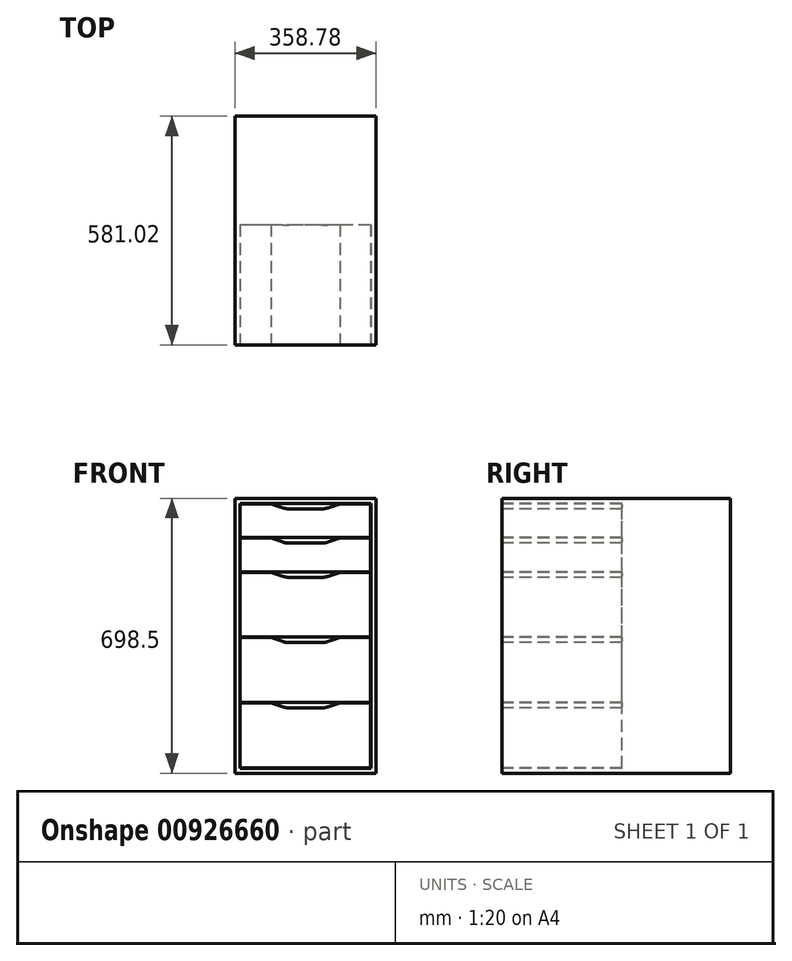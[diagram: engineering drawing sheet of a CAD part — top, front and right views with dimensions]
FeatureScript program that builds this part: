
annotation { "Feature Type Name" : "Feature", "Feature Type Description" : "" }
export const myFeature = defineFeature(function(context is Context, id is Id, definition is map)
    precondition{}
    {
        {
            var Q0;
            Q0=qCreatedBy(makeId("Front.planeOp"),FACE);
            var sketch = newSketch(context, id + "F0", { "sketchPlane" : qUnion([Q0])});
            skLineSegment(sketch, "E0.bottom", {"start": v(-48.77, 656.75) * mm, "end": v(310, 656.75) * mm});
            skLineSegment(sketch, "E0.top", {"start": v(-48.77, -41.75) * mm, "end": v(310, -41.75) * mm});
            skLineSegment(sketch, "E0.left", {"start": v(-48.77, 656.75) * mm, "end": v(-48.77, -41.75) * mm});
            skLineSegment(sketch, "E0.right", {"start": v(310, 656.75) * mm, "end": v(310, -41.75) * mm});
            skSolve(sketch);
        }
        {
            var Q0;
            Q0=makeQuery(id+"F0.imprint","IMPRINT",FACE,{"disambiguationData":[TD([[makeQuery(id+"F0.imprint","IMPRINT",EDGE,{"derivedFrom":sQuery(id+"F0.wireOp",EDGE,"E0.bottom")}),-1.0]])]});
            extrude(context, id + "F1", {"entities" : qUnion([Q0]), "depth" : 581.02 * mm, "offsetDistance" : 25.4 * mm});
        }
        {
            var Q0;
            Q0=makeQuery(id+"F1.opExtrude","CAP_FACE",FACE,{"disambiguationData":[OSD([sQuery(id+"F0.wireOp",EDGE,"E0.bottom"),sQuery(id+"F0.wireOp",EDGE,"E0.top"),sQuery(id+"F0.wireOp",EDGE,"E0.left"),sQuery(id+"F0.wireOp",EDGE,"E0.right")])],"isStart":false});
            var sketch = newSketch(context, id + "F2", { "sketchPlane" : qUnion([Q0])});
            skLineSegment(sketch, "E1.bottom", {"start": v(297.3, -29.05) * mm, "end": v(-36.07, -29.05) * mm});
            skLineSegment(sketch, "E1.top", {"start": v(297.3, 644.05) * mm, "end": v(-36.07, 644.05) * mm});
            skLineSegment(sketch, "E1.left", {"start": v(297.3, -29.05) * mm, "end": v(297.3, 644.05) * mm});
            skLineSegment(sketch, "E1.right", {"start": v(-36.07, -29.05) * mm, "end": v(-36.07, 644.05) * mm});
            skPoint(sketch, "E1.middle", {"position": v(130.62, 307.5) * mm});
            skLineSegment(sketch, "E2.bottom", {"start": v(296.04, -27.78) * mm, "end": v(-34.8, -27.78) * mm});
            skLineSegment(sketch, "E2.top", {"start": v(296.04, 642.78) * mm, "end": v(-34.8, 642.78) * mm});
            skLineSegment(sketch, "E2.left", {"start": v(296.04, -27.78) * mm, "end": v(296.04, 642.78) * mm});
            skLineSegment(sketch, "E2.right", {"start": v(-34.8, -27.78) * mm, "end": v(-34.8, 642.78) * mm});
            skSolve(sketch);
        }
        {
            var Q0;
            Q0 = qSketchRegion(id + "F2", true);
            extrude(context, id + "F3", {"entities" : qUnion([Q0]), "operationType" : NewBodyOperationType.REMOVE, "oppositeDirection" : true, "depth" : 304.8 * mm, "offsetDistance" : 25.4 * mm});
        }
        {
            var Q0;
            Q0=makeQuery(id+"F3.boolean.opBoolean","SPLIT",FACE,{"disambiguationData":[TD([makeQuery(id+"F3.opExtrude","SWEPT_FACE",FACE,{"disambiguationData":[OSD([sQuery(id+"F2.wireOp",EDGE,"E2.bottom")])]})])],"derivedFrom":makeQuery(id+"F1.opExtrude","CAP_FACE",FACE,{"disambiguationData":[OSD([sQuery(id+"F0.wireOp",EDGE,"E0.bottom"),sQuery(id+"F0.wireOp",EDGE,"E0.top"),sQuery(id+"F0.wireOp",EDGE,"E0.left"),sQuery(id+"F0.wireOp",EDGE,"E0.right")])],"isStart":false})});
            var sketch = newSketch(context, id + "F4", { "sketchPlane" : qUnion([Q0])});
            skLineSegment(sketch, "E3.bottom", {"start": v(296.04, 555.79) * mm, "end": v(-34.8, 555.79) * mm});
            skLineSegment(sketch, "E3.top", {"start": v(296.04, 557.06) * mm, "end": v(-34.8, 557.06) * mm});
            skLineSegment(sketch, "E3.left", {"start": v(296.04, 555.79) * mm, "end": v(296.04, 557.06) * mm});
            skLineSegment(sketch, "E3.right", {"start": v(-34.8, 555.79) * mm, "end": v(-34.8, 557.06) * mm});
            skPoint(sketch, "E3.middle", {"position": v(130.62, 556.42) * mm});
            skLineSegment(sketch, "E4.bottom", {"start": v(297.3, 468.8) * mm, "end": v(-36.07, 468.8) * mm});
            skLineSegment(sketch, "E4.top", {"start": v(297.3, 470.06) * mm, "end": v(-36.07, 470.06) * mm});
            skLineSegment(sketch, "E4.left", {"start": v(297.3, 468.8) * mm, "end": v(297.3, 470.06) * mm});
            skLineSegment(sketch, "E4.right", {"start": v(-36.07, 468.8) * mm, "end": v(-36.07, 470.06) * mm});
            skPoint(sketch, "E4.middle", {"position": v(130.62, 469.43) * mm});
            skLineSegment(sketch, "E5.bottom", {"start": v(296.04, 302.93) * mm, "end": v(-36.07, 302.93) * mm});
            skLineSegment(sketch, "E5.top", {"start": v(296.04, 304.2) * mm, "end": v(-36.07, 304.2) * mm});
            skLineSegment(sketch, "E5.left", {"start": v(296.04, 302.93) * mm, "end": v(296.04, 304.2) * mm});
            skLineSegment(sketch, "E5.right", {"start": v(-36.07, 302.93) * mm, "end": v(-36.07, 304.2) * mm});
            skPoint(sketch, "E5.middle", {"position": v(129.98, 303.56) * mm});
            skLineSegment(sketch, "E6.bottom", {"start": v(297.3, 137.07) * mm, "end": v(-34.8, 137.07) * mm});
            skLineSegment(sketch, "E6.top", {"start": v(297.3, 138.34) * mm, "end": v(-34.8, 138.34) * mm});
            skLineSegment(sketch, "E6.left", {"start": v(297.3, 137.07) * mm, "end": v(297.3, 138.34) * mm});
            skLineSegment(sketch, "E6.right", {"start": v(-34.8, 137.07) * mm, "end": v(-34.8, 138.34) * mm});
            skPoint(sketch, "E6.middle", {"position": v(131.25, 137.7) * mm});
            skSolve(sketch);
        }
        {
            var Q0;
            Q0 = qSketchRegion(id + "F4", true);
            extrude(context, id + "F5", {"entities" : qUnion([Q0]), "operationType" : NewBodyOperationType.REMOVE, "oppositeDirection" : true, "depth" : 304.8 * mm, "offsetDistance" : 25.4 * mm});
        }
        {
            var Q0;
            {var subQ0=makeQuery(id+"F3.opExtrude","SWEPT_FACE",FACE,{"disambiguationData":[OSD([sQuery(id+"F2.wireOp",EDGE,"E2.top")])]});Q0=makeQuery(id+"F5.boolean.opBoolean","SPLIT",FACE,{"disambiguationData":[TD([makeQuery(id+"F3.boolean.opBoolean","COPY",FACE,{"derivedFrom":subQ0})])],"derivedFrom":makeQuery(id+"F3.boolean.opBoolean","SPLIT",FACE,{"disambiguationData":[TD([makeQuery(id+"F3.opExtrude","SWEPT_FACE",FACE,{"disambiguationData":[OSD([sQuery(id+"F2.wireOp",EDGE,"E2.bottom")])]})])],"derivedFrom":makeQuery(id+"F1.opExtrude","CAP_FACE",FACE,{"disambiguationData":[OSD([sQuery(id+"F0.wireOp",EDGE,"E0.bottom"),sQuery(id+"F0.wireOp",EDGE,"E0.top"),sQuery(id+"F0.wireOp",EDGE,"E0.left"),sQuery(id+"F0.wireOp",EDGE,"E0.right")])],"isStart":false})})});}
            var sketch = newSketch(context, id + "F6", { "sketchPlane" : qUnion([Q0])});
            skLineSegment(sketch, "E7", {"start": v(43.15, 642.78) * mm, "end": v(218.09, 642.78) * mm});
            skLineSegment(sketch, "E8", {"start": v(218.09, 642.78) * mm, "end": v(179.99, 630.08) * mm});
            skLineSegment(sketch, "E9", {"start": v(179.99, 630.08) * mm, "end": v(81.25, 630.08) * mm});
            skLineSegment(sketch, "E10", {"start": v(81.25, 630.08) * mm, "end": v(43.15, 642.78) * mm});
            skSolve(sketch);
        }
        {
            var Q0;
            Q0 = qSketchRegion(id + "F6", true);
            extrude(context, id + "F7", {"entities" : qUnion([Q0]), "operationType" : NewBodyOperationType.REMOVE, "oppositeDirection" : true, "depth" : 304.8 * mm, "offsetDistance" : 25.4 * mm});
        }
        {
            var Q0;
            Q0=makeQuery(id+"F7.boolean.opBoolean","COPY",EDGE,{"derivedFrom":makeQuery(id+"F7.opExtrude","SWEPT_EDGE",EDGE,{"disambiguationData":[OSD([sQuery(id+"F2.wireOp",EDGE,"E2.top"),sQuery(id+"F6.wireOp",EDGE,"E7"),sQuery(id+"F6.wireOp",EDGE,"E10")])]})});
            var Q1;
            Q1=makeQuery(id+"F7.boolean.opBoolean","COPY",EDGE,{"derivedFrom":makeQuery(id+"F7.opExtrude","SWEPT_EDGE",EDGE,{"disambiguationData":[OSD([sQuery(id+"F6.wireOp",EDGE,"E9"),sQuery(id+"F6.wireOp",EDGE,"E10")])]})});
            var Q2;
            Q2=makeQuery(id+"F7.boolean.opBoolean","COPY",EDGE,{"derivedFrom":makeQuery(id+"F7.opExtrude","SWEPT_EDGE",EDGE,{"disambiguationData":[OSD([sQuery(id+"F6.wireOp",EDGE,"E8"),sQuery(id+"F6.wireOp",EDGE,"E9")])]})});
            var Q3;
            Q3=makeQuery(id+"F7.boolean.opBoolean","COPY",EDGE,{"derivedFrom":makeQuery(id+"F7.opExtrude","SWEPT_EDGE",EDGE,{"disambiguationData":[OSD([sQuery(id+"F2.wireOp",EDGE,"E2.top"),sQuery(id+"F6.wireOp",EDGE,"E7"),sQuery(id+"F6.wireOp",EDGE,"E8")])]})});
            fillet(context, id + "F8", {"entities" : qUnion([Q0, Q1, Q2, Q3]), "radius" : 50.8 * mm, "tangentPropagation" : true, "allowEdgeOverflow" : false});
        }
        {
            var Q0;
            Q0=makeQuery(id+"F5.boolean.opBoolean","SPLIT",FACE,{"disambiguationData":[TD([makeQuery(id+"F5.opExtrude","SWEPT_FACE",FACE,{"disambiguationData":[OSD([sQuery(id+"F4.wireOp",EDGE,"E3.bottom")])]})])],"derivedFrom":makeQuery(id+"F3.boolean.opBoolean","SPLIT",FACE,{"disambiguationData":[TD([makeQuery(id+"F3.opExtrude","SWEPT_FACE",FACE,{"disambiguationData":[OSD([sQuery(id+"F2.wireOp",EDGE,"E2.bottom")])]})])],"derivedFrom":makeQuery(id+"F1.opExtrude","CAP_FACE",FACE,{"disambiguationData":[OSD([sQuery(id+"F0.wireOp",EDGE,"E0.bottom"),sQuery(id+"F0.wireOp",EDGE,"E0.top"),sQuery(id+"F0.wireOp",EDGE,"E0.left"),sQuery(id+"F0.wireOp",EDGE,"E0.right")])],"isStart":false})})});
            var sketch = newSketch(context, id + "F9", { "sketchPlane" : qUnion([Q0])});
            skLineSegment(sketch, "E11", {"start": v(43.15, 555.79) * mm, "end": v(218.09, 555.79) * mm});
            skLineSegment(sketch, "E12", {"start": v(218.09, 555.79) * mm, "end": v(179.99, 543.09) * mm});
            skLineSegment(sketch, "E13", {"start": v(179.99, 543.09) * mm, "end": v(81.25, 543.09) * mm});
            skLineSegment(sketch, "E14", {"start": v(81.25, 543.09) * mm, "end": v(43.15, 555.79) * mm});
            skSolve(sketch);
        }
        {
            var Q0;
            Q0 = qSketchRegion(id + "F9", true);
            extrude(context, id + "F10", {"entities" : qUnion([Q0]), "operationType" : NewBodyOperationType.REMOVE, "oppositeDirection" : true, "depth" : 304.8 * mm, "offsetDistance" : 25.4 * mm});
        }
        {
            var Q0;
            Q0=makeQuery(id+"F10.boolean.opBoolean","COPY",EDGE,{"derivedFrom":makeQuery(id+"F10.opExtrude","SWEPT_EDGE",EDGE,{"disambiguationData":[OSD([sQuery(id+"F4.wireOp",EDGE,"E3.bottom"),sQuery(id+"F9.wireOp",EDGE,"E11"),sQuery(id+"F9.wireOp",EDGE,"E14")])]})});
            var Q1;
            Q1=makeQuery(id+"F10.boolean.opBoolean","COPY",EDGE,{"derivedFrom":makeQuery(id+"F10.opExtrude","SWEPT_EDGE",EDGE,{"disambiguationData":[OSD([sQuery(id+"F9.wireOp",EDGE,"E13"),sQuery(id+"F9.wireOp",EDGE,"E14")])]})});
            var Q2;
            Q2=makeQuery(id+"F10.boolean.opBoolean","COPY",EDGE,{"derivedFrom":makeQuery(id+"F10.opExtrude","SWEPT_EDGE",EDGE,{"disambiguationData":[OSD([sQuery(id+"F4.wireOp",EDGE,"E3.bottom"),sQuery(id+"F9.wireOp",EDGE,"E11"),sQuery(id+"F9.wireOp",EDGE,"E12")])]})});
            var Q3;
            Q3=makeQuery(id+"F10.boolean.opBoolean","COPY",EDGE,{"derivedFrom":makeQuery(id+"F10.opExtrude","SWEPT_EDGE",EDGE,{"disambiguationData":[OSD([sQuery(id+"F9.wireOp",EDGE,"E12"),sQuery(id+"F9.wireOp",EDGE,"E13")])]})});
            fillet(context, id + "F11", {"entities" : qUnion([Q0, Q1, Q2, Q3]), "radius" : 50.8 * mm, "tangentPropagation" : true, "allowEdgeOverflow" : false});
        }
        {
            var Q0;
            Q0=makeQuery(id+"F5.boolean.opBoolean","SPLIT",FACE,{"disambiguationData":[TD([makeQuery(id+"F5.opExtrude","SWEPT_FACE",FACE,{"disambiguationData":[OSD([sQuery(id+"F4.wireOp",EDGE,"E4.bottom")])]})])],"derivedFrom":makeQuery(id+"F3.boolean.opBoolean","SPLIT",FACE,{"disambiguationData":[TD([makeQuery(id+"F3.opExtrude","SWEPT_FACE",FACE,{"disambiguationData":[OSD([sQuery(id+"F2.wireOp",EDGE,"E2.bottom")])]})])],"derivedFrom":makeQuery(id+"F1.opExtrude","CAP_FACE",FACE,{"disambiguationData":[OSD([sQuery(id+"F0.wireOp",EDGE,"E0.bottom"),sQuery(id+"F0.wireOp",EDGE,"E0.top"),sQuery(id+"F0.wireOp",EDGE,"E0.left"),sQuery(id+"F0.wireOp",EDGE,"E0.right")])],"isStart":false})})});
            var sketch = newSketch(context, id + "F12", { "sketchPlane" : qUnion([Q0])});
            skLineSegment(sketch, "E15", {"start": v(43.15, 468.8) * mm, "end": v(218.09, 468.8) * mm});
            skLineSegment(sketch, "E16", {"start": v(218.09, 468.8) * mm, "end": v(179.99, 456.1) * mm});
            skLineSegment(sketch, "E17", {"start": v(179.99, 456.1) * mm, "end": v(81.25, 456.1) * mm});
            skLineSegment(sketch, "E18", {"start": v(81.25, 456.1) * mm, "end": v(43.15, 468.8) * mm});
            skSolve(sketch);
        }
        {
            var Q0;
            Q0 = qSketchRegion(id + "F12", true);
            extrude(context, id + "F13", {"entities" : qUnion([Q0]), "operationType" : NewBodyOperationType.REMOVE, "oppositeDirection" : true, "depth" : 304.8 * mm, "offsetDistance" : 25.4 * mm});
        }
        {
            var Q0;
            Q0=makeQuery(id+"F13.boolean.opBoolean","COPY",EDGE,{"derivedFrom":makeQuery(id+"F13.opExtrude","SWEPT_EDGE",EDGE,{"disambiguationData":[OSD([sQuery(id+"F4.wireOp",EDGE,"E4.bottom"),sQuery(id+"F12.wireOp",EDGE,"E15"),sQuery(id+"F12.wireOp",EDGE,"E18")])]})});
            var Q1;
            Q1=makeQuery(id+"F13.boolean.opBoolean","COPY",EDGE,{"derivedFrom":makeQuery(id+"F13.opExtrude","SWEPT_EDGE",EDGE,{"disambiguationData":[OSD([sQuery(id+"F12.wireOp",EDGE,"E17"),sQuery(id+"F12.wireOp",EDGE,"E18")])]})});
            var Q2;
            Q2=makeQuery(id+"F13.boolean.opBoolean","COPY",EDGE,{"derivedFrom":makeQuery(id+"F13.opExtrude","SWEPT_EDGE",EDGE,{"disambiguationData":[OSD([sQuery(id+"F12.wireOp",EDGE,"E16"),sQuery(id+"F12.wireOp",EDGE,"E17")])]})});
            var Q3;
            Q3=makeQuery(id+"F13.boolean.opBoolean","COPY",EDGE,{"derivedFrom":makeQuery(id+"F13.opExtrude","SWEPT_EDGE",EDGE,{"disambiguationData":[OSD([sQuery(id+"F4.wireOp",EDGE,"E4.bottom"),sQuery(id+"F12.wireOp",EDGE,"E15"),sQuery(id+"F12.wireOp",EDGE,"E16")])]})});
            fillet(context, id + "F14", {"entities" : qUnion([Q0, Q1, Q2, Q3]), "radius" : 50.8 * mm, "tangentPropagation" : true, "allowEdgeOverflow" : false});
        }
        {
            var Q0;
            Q0=makeQuery(id+"F5.boolean.opBoolean","SPLIT",FACE,{"disambiguationData":[TD([makeQuery(id+"F5.opExtrude","SWEPT_FACE",FACE,{"disambiguationData":[OSD([sQuery(id+"F4.wireOp",EDGE,"E5.bottom")])]})])],"derivedFrom":makeQuery(id+"F3.boolean.opBoolean","SPLIT",FACE,{"disambiguationData":[TD([makeQuery(id+"F3.opExtrude","SWEPT_FACE",FACE,{"disambiguationData":[OSD([sQuery(id+"F2.wireOp",EDGE,"E2.bottom")])]})])],"derivedFrom":makeQuery(id+"F1.opExtrude","CAP_FACE",FACE,{"disambiguationData":[OSD([sQuery(id+"F0.wireOp",EDGE,"E0.bottom"),sQuery(id+"F0.wireOp",EDGE,"E0.top"),sQuery(id+"F0.wireOp",EDGE,"E0.left"),sQuery(id+"F0.wireOp",EDGE,"E0.right")])],"isStart":false})})});
            var sketch = newSketch(context, id + "F15", { "sketchPlane" : qUnion([Q0])});
            skLineSegment(sketch, "E19", {"start": v(43.15, 302.93) * mm, "end": v(218.09, 302.93) * mm});
            skLineSegment(sketch, "E20", {"start": v(218.09, 302.93) * mm, "end": v(179.99, 290.23) * mm});
            skLineSegment(sketch, "E21", {"start": v(179.99, 290.23) * mm, "end": v(81.25, 290.23) * mm});
            skLineSegment(sketch, "E22", {"start": v(81.25, 290.23) * mm, "end": v(43.15, 302.93) * mm});
            skSolve(sketch);
        }
        {
            var Q0;
            Q0 = qSketchRegion(id + "F15", true);
            extrude(context, id + "F16", {"entities" : qUnion([Q0]), "operationType" : NewBodyOperationType.REMOVE, "oppositeDirection" : true, "depth" : 304.8 * mm, "offsetDistance" : 25.4 * mm});
        }
        {
            var Q0;
            Q0=makeQuery(id+"F16.boolean.opBoolean","COPY",EDGE,{"derivedFrom":makeQuery(id+"F16.opExtrude","SWEPT_EDGE",EDGE,{"disambiguationData":[OSD([sQuery(id+"F4.wireOp",EDGE,"E5.bottom"),sQuery(id+"F15.wireOp",EDGE,"E19"),sQuery(id+"F15.wireOp",EDGE,"E22")])]})});
            var Q1;
            Q1=makeQuery(id+"F16.boolean.opBoolean","COPY",EDGE,{"derivedFrom":makeQuery(id+"F16.opExtrude","SWEPT_EDGE",EDGE,{"disambiguationData":[OSD([sQuery(id+"F15.wireOp",EDGE,"E21"),sQuery(id+"F15.wireOp",EDGE,"E22")])]})});
            var Q2;
            Q2=makeQuery(id+"F16.boolean.opBoolean","COPY",EDGE,{"derivedFrom":makeQuery(id+"F16.opExtrude","SWEPT_EDGE",EDGE,{"disambiguationData":[OSD([sQuery(id+"F15.wireOp",EDGE,"E20"),sQuery(id+"F15.wireOp",EDGE,"E21")])]})});
            var Q3;
            Q3=makeQuery(id+"F16.boolean.opBoolean","COPY",EDGE,{"derivedFrom":makeQuery(id+"F16.opExtrude","SWEPT_EDGE",EDGE,{"disambiguationData":[OSD([sQuery(id+"F4.wireOp",EDGE,"E5.bottom"),sQuery(id+"F15.wireOp",EDGE,"E19"),sQuery(id+"F15.wireOp",EDGE,"E20")])]})});
            fillet(context, id + "F17", {"entities" : qUnion([Q0, Q1, Q2, Q3]), "radius" : 50.8 * mm, "tangentPropagation" : true, "allowEdgeOverflow" : false});
        }
        {
            var Q0;
            {var subQ0=makeQuery(id+"F3.opExtrude","SWEPT_FACE",FACE,{"disambiguationData":[OSD([sQuery(id+"F2.wireOp",EDGE,"E2.bottom")])]});Q0=makeQuery(id+"F5.boolean.opBoolean","SPLIT",FACE,{"disambiguationData":[TD([makeQuery(id+"F3.boolean.opBoolean","COPY",FACE,{"derivedFrom":subQ0})])],"derivedFrom":makeQuery(id+"F3.boolean.opBoolean","SPLIT",FACE,{"disambiguationData":[TD([subQ0])],"derivedFrom":makeQuery(id+"F1.opExtrude","CAP_FACE",FACE,{"disambiguationData":[OSD([sQuery(id+"F0.wireOp",EDGE,"E0.bottom"),sQuery(id+"F0.wireOp",EDGE,"E0.top"),sQuery(id+"F0.wireOp",EDGE,"E0.left"),sQuery(id+"F0.wireOp",EDGE,"E0.right")])],"isStart":false})})});}
            var sketch = newSketch(context, id + "F18", { "sketchPlane" : qUnion([Q0])});
            skLineSegment(sketch, "E23", {"start": v(43.15, 137.07) * mm, "end": v(218.09, 137.07) * mm});
            skLineSegment(sketch, "E24", {"start": v(218.09, 137.07) * mm, "end": v(179.99, 124.37) * mm});
            skLineSegment(sketch, "E25", {"start": v(179.99, 124.37) * mm, "end": v(81.25, 124.37) * mm});
            skLineSegment(sketch, "E26", {"start": v(81.25, 124.37) * mm, "end": v(43.15, 137.07) * mm});
            skSolve(sketch);
        }
        {
            var Q0;
            Q0 = qSketchRegion(id + "F18", true);
            extrude(context, id + "F19", {"entities" : qUnion([Q0]), "operationType" : NewBodyOperationType.REMOVE, "oppositeDirection" : true, "depth" : 304.8 * mm, "offsetDistance" : 25.4 * mm});
        }
        {
            var Q0;
            Q0=makeQuery(id+"F19.boolean.opBoolean","COPY",EDGE,{"derivedFrom":makeQuery(id+"F19.opExtrude","SWEPT_EDGE",EDGE,{"disambiguationData":[OSD([sQuery(id+"F4.wireOp",EDGE,"E6.bottom"),sQuery(id+"F18.wireOp",EDGE,"E23"),sQuery(id+"F18.wireOp",EDGE,"E26")])]})});
            var Q1;
            Q1=makeQuery(id+"F19.boolean.opBoolean","COPY",EDGE,{"derivedFrom":makeQuery(id+"F19.opExtrude","SWEPT_EDGE",EDGE,{"disambiguationData":[OSD([sQuery(id+"F18.wireOp",EDGE,"E25"),sQuery(id+"F18.wireOp",EDGE,"E26")])]})});
            var Q2;
            Q2=makeQuery(id+"F19.boolean.opBoolean","COPY",EDGE,{"derivedFrom":makeQuery(id+"F19.opExtrude","SWEPT_EDGE",EDGE,{"disambiguationData":[OSD([sQuery(id+"F18.wireOp",EDGE,"E24"),sQuery(id+"F18.wireOp",EDGE,"E25")])]})});
            var Q3;
            Q3=makeQuery(id+"F19.boolean.opBoolean","COPY",EDGE,{"derivedFrom":makeQuery(id+"F19.opExtrude","SWEPT_EDGE",EDGE,{"disambiguationData":[OSD([sQuery(id+"F4.wireOp",EDGE,"E6.bottom"),sQuery(id+"F18.wireOp",EDGE,"E23"),sQuery(id+"F18.wireOp",EDGE,"E24")])]})});
            fillet(context, id + "F20", {"entities" : qUnion([Q0, Q1, Q2, Q3]), "radius" : 50.8 * mm, "tangentPropagation" : true, "allowEdgeOverflow" : false});
        }
    });
